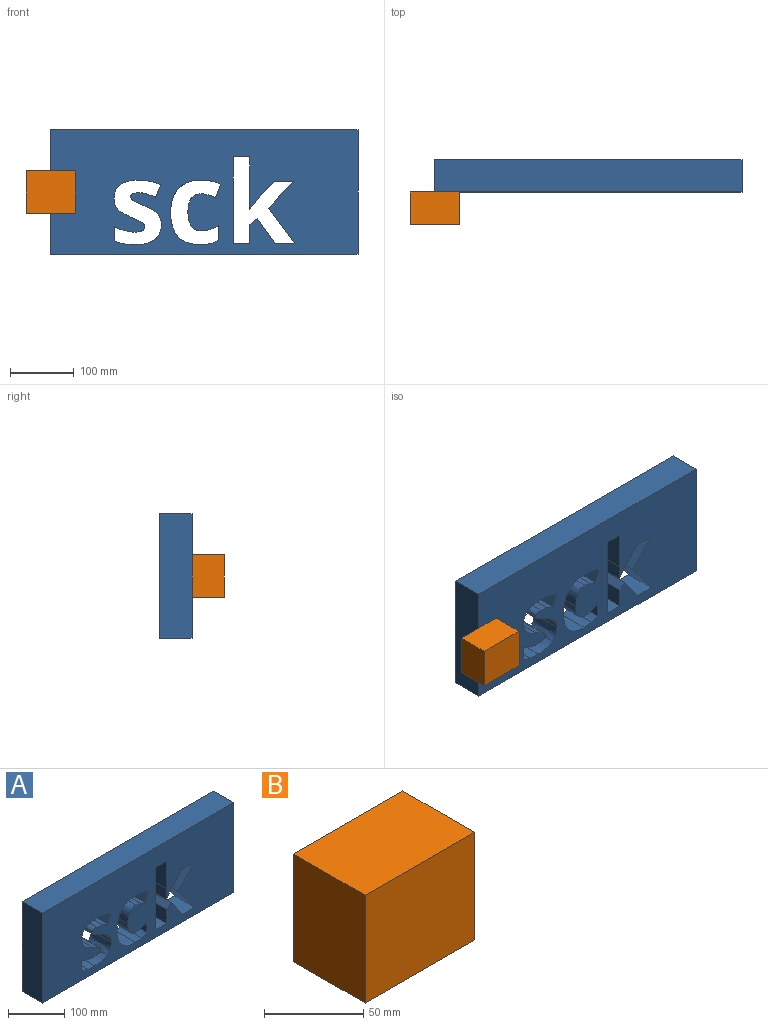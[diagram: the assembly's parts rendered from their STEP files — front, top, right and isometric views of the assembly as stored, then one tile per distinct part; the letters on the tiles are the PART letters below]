
ASSEMBLY  parts=2 mates=1
PART A: 61 faces, bbox 482.7x50.8x195.6 mm
  f0: plane 482.66x195.62mm, normal (0,-1,0), area 78724.8mm2, adj f2,f3,f4,f5,f6,f7,f8,f9
  f1: plane 482.66x195.62mm, normal (0,1,0), area 78724.8mm2, adj f2,f3,f4,f5,f6,f7,f8,f9
  f2: plane 482.66x50.8mm, normal (0,0,1), area 24519.2mm2, adj f0,f1,f3,f5
  f3: plane 195.62x50.8mm, normal (-1,0,0), area 9937.4mm2, adj f0,f1,f2,f4
  f4: plane 482.66x50.8mm, normal (0,0,-1), area 24519.2mm2, adj f0,f1,f3,f5
  f5: plane 195.62x50.8mm, normal (1,0,0), area 9937.4mm2, adj f0,f1,f2,f4
  f6: plane 50.8x14.85mm, normal (0.79,0,-0.62), area 957.2mm2, adj f0,f1,f7,f20
  f7: plane 50.8x0.36mm, normal (0,0,-1), area 18.5mm2, adj f0,f1,f6,f8
  f8: plane 50.8x22.2mm, normal (-1,0,0.06), area 1130mm2, adj f0,f1,f7,f9
  f9: plane 60.64x50.8mm, normal (-1,0,0), area 3080.7mm2, adj f0,f1,f8,f10
  f10: plane 50.8x26.65mm, normal (0,0,-1), area 1353.6mm2, adj f0,f1,f9,f11
  f11: plane 135.96x50.8mm, normal (1,0,0), area 6907mm2, adj f0,f1,f10,f12
  f12: plane 50.8x26.65mm, normal (0,0,1), area 1353.6mm2, adj f0,f1,f11,f13
  f13: plane 50.8x30.42mm, normal (-1,0,0), area 1545.3mm2, adj f0,f1,f12,f14
  f14: plane 50.8x11.46mm, normal (-0.62,0,0.78), area 745.7mm2, adj f0,f1,f13,f15
  f15: plane 50.8x39.59mm, normal (0.82,0,0.58), area 2467mm2, adj f0,f1,f14,f16
  f16: plane 50.8x30.75mm, normal (0,0,1), area 1562.3mm2, adj f0,f1,f15,f17
  f17: plane 55.3x50.8mm, normal (-0.8,0,-0.6), area 3501.9mm2, adj f0,f1,f16,f18
  f18: plane 50.8x42.39mm, normal (-0.74,0,0.68), area 2918.4mm2, adj f0,f1,f17,f19
  f19: plane 50.8x30.06mm, normal (0,0,-1), area 1526.8mm2, adj f0,f1,f18,f20
  f20: plane 50.8x29.72mm, normal (0.74,0,-0.68), area 2051.6mm2, adj f0,f1,f6,f19
  f21: extruded ~50.8x50.07mm, area 3946.4mm2, adj f0,f1,f22,f34
  f22: extruded ~50.8x16.64mm, area 850.8mm2, adj f0,f1,f21,f23
  f23: extruded ~50.8x13.06mm, area 726.9mm2, adj f0,f1,f22,f24
  f24: plane 50.8x22.81mm, normal (-1,0,0), area 1159mm2, adj f0,f1,f23,f25
  f25: extruded ~50.8x13.1mm, area 744.1mm2, adj f0,f1,f24,f26
  f26: extruded ~50.8x14.25mm, area 734mm2, adj f0,f1,f25,f27
  f27: extruded ~50.8x28.66mm, area 2049.3mm2, adj f0,f1,f26,f28
  f28: extruded ~50.8x29.55mm, area 2088.4mm2, adj f0,f1,f27,f29
  f29: extruded ~50.8x10.83mm, area 558.5mm2, adj f0,f1,f28,f30
  f30: extruded ~50.8x11.7mm, area 631.2mm2, adj f0,f1,f29,f31
  f31: plane 50.8x20.63mm, normal (-0.93,0,0.36), area 1122.1mm2, adj f0,f1,f30,f32
  f32: extruded ~50.8x30.42mm, area 1595.6mm2, adj f0,f1,f31,f33
  f33: extruded ~50.8x35.55mm, area 1982.1mm2, adj f0,f1,f32,f34
  f34: extruded ~50.8x38.05mm, area 2083.3mm2, adj f0,f1,f21,f33
  f35: extruded ~50.8x22.91mm, area 1329.9mm2, adj f0,f1,f36,f60
  f36: extruded ~50.8x12.48mm, area 652.8mm2, adj f0,f1,f35,f37
  f37: extruded ~50.8x9.25mm, area 623mm2, adj f0,f1,f36,f38
  f38: extruded ~50.8x16.76mm, area 960.6mm2, adj f0,f1,f37,f39
  f39: extruded ~50.8x16.66mm, area 935.4mm2, adj f0,f1,f38,f40
  f40: extruded ~50.8x6.21mm, area 385.6mm2, adj f0,f1,f39,f41
  f41: extruded ~50.8x11.8mm, area 762.5mm2, adj f0,f1,f40,f42
  f42: extruded ~50.8x13.03mm, area 672.4mm2, adj f0,f1,f41,f43
  f43: extruded ~50.8x13.73mm, area 745mm2, adj f0,f1,f42,f44
  f44: plane 50.8x19.21mm, normal (-0.92,0,0.39), area 1057.5mm2, adj f0,f1,f43,f45
  f45: extruded ~50.8x34.33mm, area 1801.5mm2, adj f0,f1,f44,f46
  f46: extruded ~50.8x28.62mm, area 1521.3mm2, adj f0,f1,f45,f47
  f47: extruded ~50.8x20.14mm, area 1193.5mm2, adj f0,f1,f46,f48
  f48: extruded ~50.8x12.78mm, area 665.4mm2, adj f0,f1,f47,f49
  f49: extruded ~50.8x9.23mm, area 616.4mm2, adj f0,f1,f48,f50
  f50: extruded ~50.8x16.57mm, area 954mm2, adj f0,f1,f49,f51
  f51: extruded ~50.8x12.57mm, area 703.1mm2, adj f0,f1,f50,f52
  f52: extruded ~50.8x6.64mm, area 407.8mm2, adj f0,f1,f51,f53
  f53: extruded ~50.8x5.13mm, area 285.9mm2, adj f0,f1,f52,f54
  f54: extruded ~50.8x14.51mm, area 957.5mm2, adj f0,f1,f53,f55
  f55: extruded ~50.8x16.38mm, area 843mm2, adj f0,f1,f54,f56
  f56: extruded ~50.8x16.72mm, area 901.3mm2, adj f0,f1,f55,f57
  f57: plane 50.8x22mm, normal (1,0,0), area 1117.8mm2, adj f0,f1,f56,f58
  f58: extruded ~50.8x14.06mm, area 747.7mm2, adj f0,f1,f57,f59
  f59: extruded ~50.8x18.17mm, area 927.5mm2, adj f0,f1,f58,f60
  f60: extruded ~50.8x31.24mm, area 1664.5mm2, adj f0,f1,f35,f59
PART B: 6 faces, bbox 77.6x50.8x66.3 mm
  f0: plane 77.63x50.8mm, normal (0,0,1), area 3943.6mm2, adj f1,f3,f4,f5
  f1: plane 66.31x50.8mm, normal (-1,0,0), area 3368.5mm2, adj f0,f2,f4,f5
  f2: plane 77.63x50.8mm, normal (0,0,-1), area 3943.6mm2, adj f1,f3,f4,f5
  f3: plane 66.31x50.8mm, normal (1,0,0), area 3368.5mm2, adj f0,f2,f4,f5
  f4: plane 77.63x66.31mm, normal (0,-1,0), area 5147.5mm2, adj f0,f1,f2,f3
  f5: plane 77.63x66.31mm, normal (0,1,0), area 5147.5mm2, adj f0,f1,f2,f3
PLACE A t=(-32.65,49.54,-16.41)mm
PLACE B t=(-262.99,-1.26,-22.59)mm
MATE fastened A.f0 <-> B.f5  axis (0,-1,0) through (-268.27,24.14,-12.76)mm
